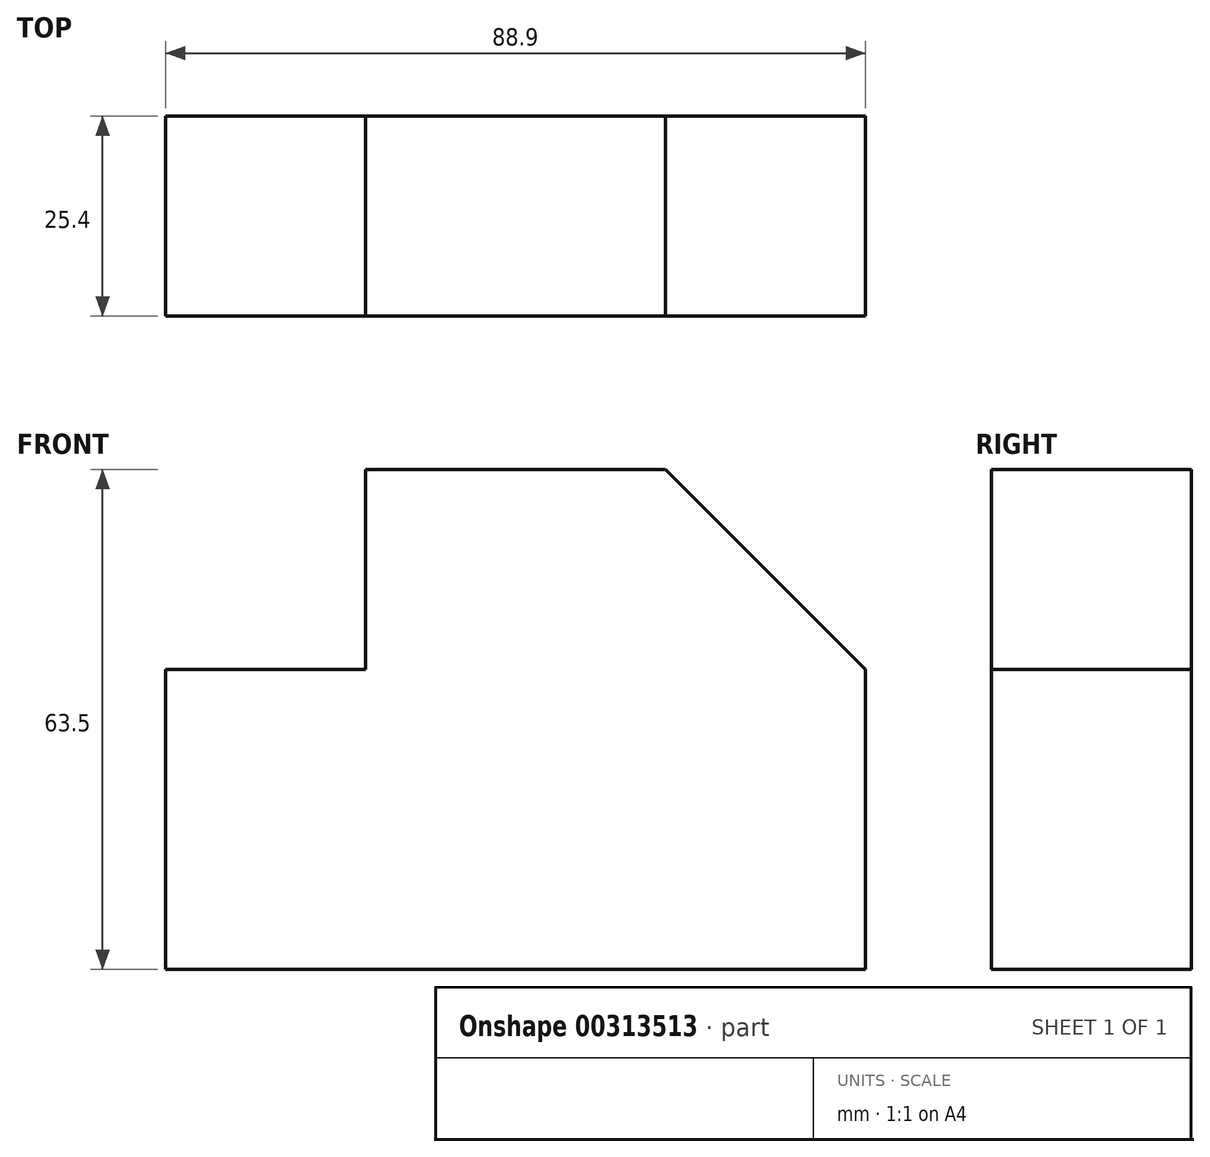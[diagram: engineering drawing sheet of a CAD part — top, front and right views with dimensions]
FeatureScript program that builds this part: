
annotation { "Feature Type Name" : "Feature", "Feature Type Description" : "" }
export const myFeature = defineFeature(function(context is Context, id is Id, definition is map)
    precondition{}
    {
        {
            var Q0;
            Q0=qCreatedBy(makeId("Front.planeOp"),FACE);
            var sketch = newSketch(context, id + "F0", { "sketchPlane" : qUnion([Q0])});
            skLineSegment(sketch, "E0", {"start": v(-46.96, -40.75) * mm, "end": v(41.94, -40.75) * mm});
            skLineSegment(sketch, "E1", {"start": v(-46.96, -40.75) * mm, "end": v(-46.96, -2.65) * mm});
            skLineSegment(sketch, "E2", {"start": v(-46.96, -2.65) * mm, "end": v(-21.56, -2.65) * mm});
            skLineSegment(sketch, "E3", {"start": v(-21.56, -2.65) * mm, "end": v(-21.56, 22.75) * mm});
            skLineSegment(sketch, "E4", {"start": v(-21.56, 22.75) * mm, "end": v(16.54, 22.75) * mm});
            skLineSegment(sketch, "E5", {"start": v(41.94, -40.75) * mm, "end": v(41.94, -2.65) * mm});
            skLineSegment(sketch, "E6", {"start": v(16.54, 22.75) * mm, "end": v(41.94, -2.65) * mm});
            skSolve(sketch);
        }
        {
            var Q0;
            Q0=makeQuery(id+"F0.imprint","IMPRINT",FACE,{"disambiguationData":[TD([[makeQuery(id+"F0.imprint","IMPRINT",EDGE,{"derivedFrom":sQuery(id+"F0.wireOp",EDGE,"E0")}),1.0]])]});
            extrude(context, id + "F1", {"entities" : qUnion([Q0]), "depth" : 25.4 * mm});
        }
    });
